# Revit family: Sanitary_Taps&Mixers_Zurn_Z826B1-XL
name_source: partatom
category: Plumbing Fixtures
units: mm (PartAtom-declared; Revit-internal decimal feet)

## family parameters
Cut with Voids When Loaded = No
Host = Face
Maintain Annotation Orientation = No
OmniClass Number = 23.45.55.17
OmniClass Title = Mixing Faucets
Part Type = Normal
Room Calculation Point = No
Round Connector Dimension = Use Radius
Shared = No

## types (9) — shared parameters
ADA Compliance = Yes
Assembly Code = D2010
CW Connection = Yes
CWFU = 1
Default Elevation = 34"
Description = Laboratory Faucet - Double
HW Connection = Yes
Height from Spout Base to Areator = 9 1/2"
Inlet Connection Size (inch) = 1/2"
Lead- Free Compliant = Yes
Main Material = Brass - Zurn - Polished Chrome-Finish
Manufacturer = Zurn Water, LLC
Manufacturer Brand = Zurn
Model = Z826B1-XL
Modified Date = 09/01/2025
Product Documentation Link = https://files.zurn.com
Product Page URL = https://www.zurn.com
Product data URL = https://www.bimobject.com
Spout Height from Base = 13 1/2"
Spout length = 5 1/2"
URL = http://www.zurn.com
Vent Connection = No
Waste Connection = No
Water Sense Compliance = No
Width of Handle = 2 1/2"
zero-valued in all types: HWFU, WFU

## per-type parameters (varying)
| type | Flow  Rate | Types of Outlet |
| Z826B1-XL-2F (2.2 GPM AERATOR OUTLET) | 2 GPM | AERATOR |
| Z826B1-XL-3F (0.5 GPM SPRAY OUTLET) | 1 GPM | SPRAY |
| Z826B1-XL-4F (2.2 GPM LAMINAR OUTLET) | 2 GPM | LAMINAR |
| Z826B1-XL-16F (1.0 GPM SPRAY OUTLET) | 1 GPM | SPRAY |
| Z826B1-XL-17F (1.5 GPM AERATOR OUTLET) | 2 GPM | AERATOR |
| Z826B1-XL-18F (1.5 GPM LAMINAR OUTLET) | 2 GPM | LAMINAR |
| Z826B1-XL-22F (1.0 GPM LAMINAR OUTLET) | 1 GPM | LAMINAR |
| Z826B1-XL-25F (0.35 GPM SPRAY OUTLET) | 0 GPM | SPRAY |
| Z826B1-XL-28F (0.5 GPM LAMINAR OUTLET) | 1 GPM | LAMINAR |

## geometry (parser evidence)
native form markers: Blend x4, Sweep x5
no freeform markers — native parametric forms only
